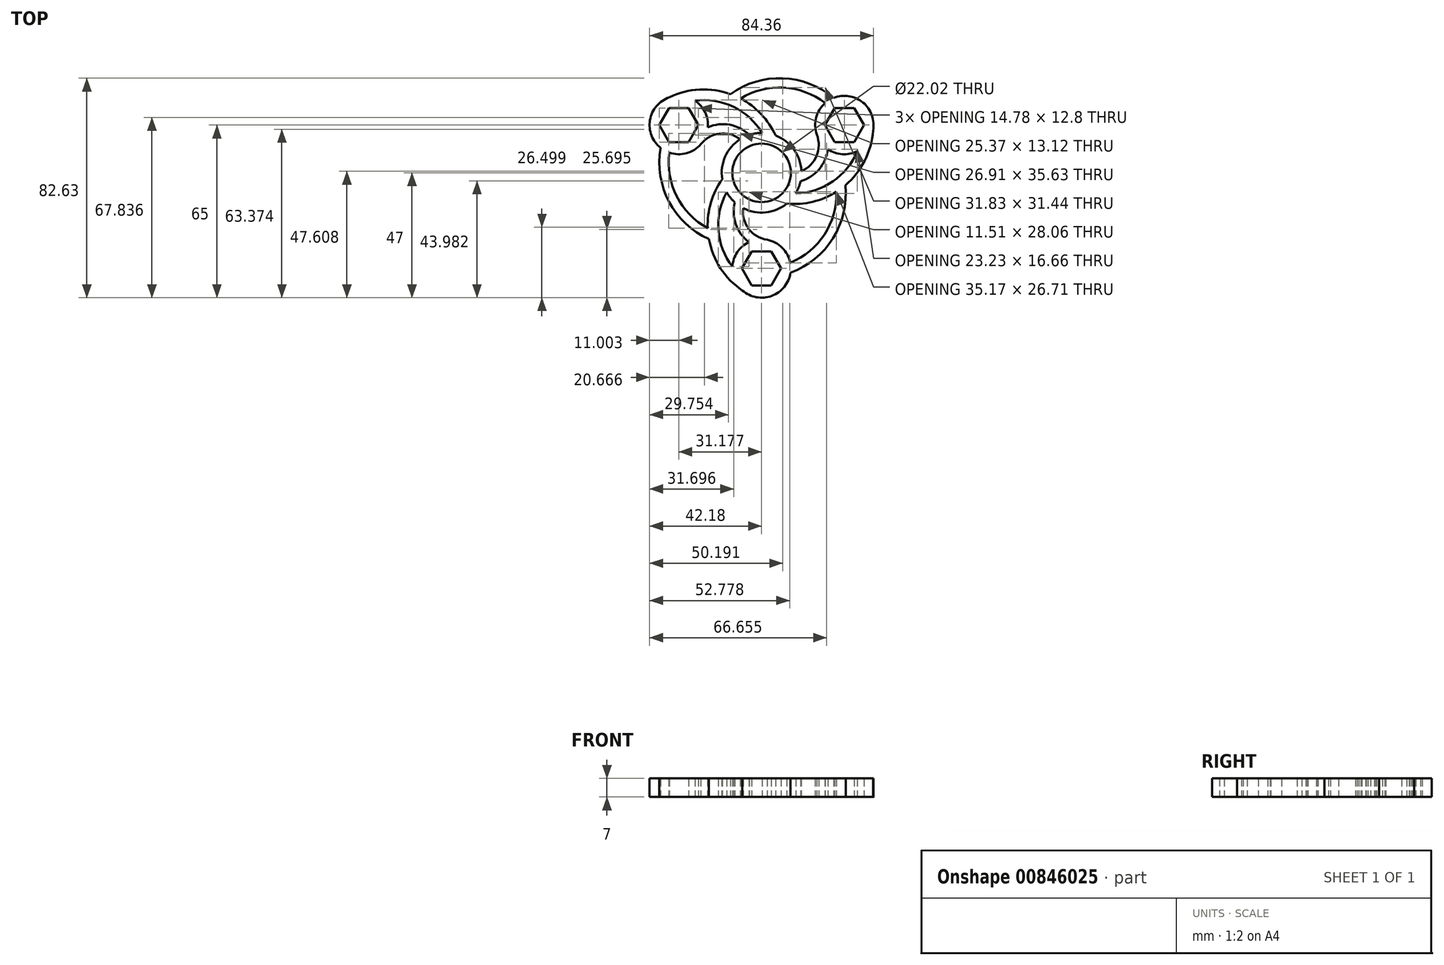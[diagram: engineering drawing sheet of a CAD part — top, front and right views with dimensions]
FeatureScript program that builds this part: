
annotation { "Feature Type Name" : "Feature", "Feature Type Description" : "" }
export const myFeature = defineFeature(function(context is Context, id is Id, definition is map)
    precondition{}
    {
        {
            var Q0;
            Q0=qCreatedBy(makeId("Top.planeOp"),FACE);
            var sketch = newSketch(context, id + "F0", { "sketchPlane" : qUnion([Q0])});
            skCircle(sketch, "E0", {"center": v(0, 0) * mm, "radius": 11.01 * mm});
            skCircle(sketch, "E1", {"center": v(0, 0) * mm, "radius": 15 * mm});
            skCircle(sketch, "E2", {"center": v(0, -36) * mm, "radius": 11 * mm});
            skCircle(sketch, "E3.1.0", {"center": v(31.18, 18) * mm, "radius": 11 * mm});
            skCircle(sketch, "E3.2.0", {"center": v(-31.18, 18) * mm, "radius": 11 * mm});
            skArc(sketch, "E4", {"start": v(5.28, 14.04) * mm, "mid": v(-11.7, 29.65) * mm, "end": v(-34.73, 28.41) * mm});
            skArc(sketch, "E5.0", {"start": v(2.32, 10.76) * mm, "mid": v(-8.54, 23.75) * mm, "end": v(-25.11, 27.18) * mm});
            skArc(sketch, "E6.1.0", {"start": v(-14.8, -2.44) * mm, "mid": v(-19.83, -24.95) * mm, "end": v(-7.24, -44.28) * mm});
            skArc(sketch, "E6.1.1", {"start": v(-10.48, -3.37) * mm, "mid": v(-16.3, -19.27) * mm, "end": v(-10.98, -35.33) * mm});
            skArc(sketch, "E6.2.0", {"start": v(9.52, -11.6) * mm, "mid": v(31.52, -4.7) * mm, "end": v(41.97, 15.87) * mm});
            skArc(sketch, "E6.2.1", {"start": v(8.16, -7.39) * mm, "mid": v(24.83, -4.48) * mm, "end": v(36.09, 8.16) * mm});
            skArc(sketch, "E7", {"start": v(-4.6, 14.28) * mm, "mid": v(-11.97, 18.1) * mm, "end": v(-20.21, 17.13) * mm});
            skArc(sketch, "E8.0", {"start": v(-8.06, 12.65) * mm, "mid": v(-15.85, 14.74) * mm, "end": v(-22.88, 10.78) * mm});
            skArc(sketch, "E9.1.0", {"start": v(-10.06, -11.12) * mm, "mid": v(-9.69, -19.41) * mm, "end": v(-4.73, -26.07) * mm});
            skArc(sketch, "E9.1.1", {"start": v(-6.93, -13.3) * mm, "mid": v(-4.84, -21.1) * mm, "end": v(2.1, -25.2) * mm});
            skArc(sketch, "E9.2.0", {"start": v(14.66, -3.15) * mm, "mid": v(21.65, 1.32) * mm, "end": v(24.94, 8.94) * mm});
            skArc(sketch, "E9.2.1", {"start": v(14.99, 0.66) * mm, "mid": v(20.7, 6.36) * mm, "end": v(20.77, 14.42) * mm});
            skArc(sketch, "E10", {"start": v(-37.98, 9.36) * mm, "mid": v(-34.81, -10.93) * mm, "end": v(-19.83, -24.96) * mm});
            skArc(sketch, "E11.0", {"start": v(-34.72, 7.59) * mm, "mid": v(-31.93, -8.88) * mm, "end": v(-20.28, -20.83) * mm});
            skArc(sketch, "E12.1.0", {"start": v(10.79, -33.86) * mm, "mid": v(23.65, -23.21) * mm, "end": v(28.18, -7.14) * mm});
            skArc(sketch, "E12.1.1", {"start": v(10.89, -37.57) * mm, "mid": v(26.87, -24.68) * mm, "end": v(31.53, -4.7) * mm});
            skArc(sketch, "E12.2.0", {"start": v(23.93, 26.27) * mm, "mid": v(8.28, 32.1) * mm, "end": v(-7.9, 27.98) * mm});
            skArc(sketch, "E12.2.1", {"start": v(27.1, 28.21) * mm, "mid": v(7.94, 35.61) * mm, "end": v(-11.7, 29.65) * mm});
            skCircle(sketch, "E13.cCircle", {"center": v(-31.18, 18) * mm, "radius": 6.4 * mm, "construction": true});
            skLineSegment(sketch, "E13.0", {"start": v(-23.79, 18) * mm, "end": v(-27.48, 11.6) * mm});
            skLineSegment(sketch, "E13.1", {"start": v(-27.48, 11.6) * mm, "end": v(-34.87, 11.6) * mm});
            skLineSegment(sketch, "E13.2", {"start": v(-34.87, 11.6) * mm, "end": v(-38.57, 18) * mm});
            skLineSegment(sketch, "E13.3", {"start": v(-38.57, 18) * mm, "end": v(-34.87, 24.4) * mm});
            skLineSegment(sketch, "E13.4", {"start": v(-34.87, 24.4) * mm, "end": v(-27.48, 24.4) * mm});
            skLineSegment(sketch, "E13.5", {"start": v(-27.48, 24.4) * mm, "end": v(-23.79, 18) * mm});
            skPoint(sketch, "E13.0.midPoint", {"position": v(-25.63, 14.8) * mm});
            skCircle(sketch, "E14.1.0", {"center": v(0, -36) * mm, "radius": 6.4 * mm, "construction": true});
            skLineSegment(sketch, "E14.1.1", {"start": v(-3.7, -42.4) * mm, "end": v(-7.4, -36) * mm});
            skLineSegment(sketch, "E14.1.2", {"start": v(3.7, -42.4) * mm, "end": v(-3.7, -42.4) * mm});
            skLineSegment(sketch, "E14.1.3", {"start": v(7.4, -36) * mm, "end": v(3.7, -42.4) * mm});
            skLineSegment(sketch, "E14.1.4", {"start": v(3.7, -29.6) * mm, "end": v(7.4, -36) * mm});
            skLineSegment(sketch, "E14.1.5", {"start": v(-3.7, -29.6) * mm, "end": v(3.7, -29.6) * mm});
            skLineSegment(sketch, "E14.1.6", {"start": v(-7.4, -36) * mm, "end": v(-3.7, -29.6) * mm});
            skCircle(sketch, "E14.2.0", {"center": v(31.18, 18) * mm, "radius": 6.4 * mm, "construction": true});
            skLineSegment(sketch, "E14.2.1", {"start": v(38.57, 18) * mm, "end": v(34.87, 11.6) * mm});
            skLineSegment(sketch, "E14.2.2", {"start": v(34.87, 24.4) * mm, "end": v(38.57, 18) * mm});
            skLineSegment(sketch, "E14.2.3", {"start": v(27.48, 24.4) * mm, "end": v(34.87, 24.4) * mm});
            skLineSegment(sketch, "E14.2.4", {"start": v(23.79, 18) * mm, "end": v(27.48, 24.4) * mm});
            skLineSegment(sketch, "E14.2.5", {"start": v(27.48, 11.6) * mm, "end": v(23.79, 18) * mm});
            skLineSegment(sketch, "E14.2.6", {"start": v(34.87, 11.6) * mm, "end": v(27.48, 11.6) * mm});
            skSolve(sketch);
        }
        {
            var Q0;
            {var subQ0=sQuery(id+"F0.wireOp",EDGE,"E3.2.0");var subQ1=makeQuery(id+"F0.imprint","INTERSECT",VERTEX,{"derivedFrom":[subQ0,sQuery(id+"F0.wireOp",EDGE,"E7")]});Q0=makeQuery(id+"F0.imprint","IMPRINT",FACE,{"disambiguationData":[TD([[makeQuery(id+"F0.imprint","IMPRINT",EDGE,{"disambiguationData":[TD([[subQ1,1.0]])],"derivedFrom":subQ0}),1.0]])]});}
            var Q1;
            {var subQ0=sQuery(id+"F0.wireOp",EDGE,"E4");Q1=makeQuery(id+"F0.imprint","IMPRINT",FACE,{"disambiguationData":[TD([[makeQuery(id+"F0.imprint","IMPRINT",EDGE,{"derivedFrom":subQ0}),1.0]])]});}
            var Q2;
            {var subQ4=sQuery(id+"F0.wireOp",EDGE,"E5.0");var subQ6=sQuery(id+"F0.wireOp",EDGE,"E0");var subQ7=makeQuery(id+"F0.imprint","INTERSECT",VERTEX,{"derivedFrom":[subQ6,subQ4]});Q2=makeQuery(id+"F0.imprint","IMPRINT",FACE,{"disambiguationData":[TD([[makeQuery(id+"F0.imprint","IMPRINT",EDGE,{"disambiguationData":[TD([[subQ7,-1.0]])],"derivedFrom":subQ6}),-1.0]])]});}
            var Q3;
            {var subQ0=sQuery(id+"F0.wireOp",EDGE,"E5.0");var subQ1=sQuery(id+"F0.wireOp",EDGE,"E0");var subQ2=makeQuery(id+"F0.imprint","INTERSECT",VERTEX,{"derivedFrom":[subQ1,subQ0]});Q3=makeQuery(id+"F0.imprint","IMPRINT",FACE,{"disambiguationData":[TD([[makeQuery(id+"F0.imprint","IMPRINT",EDGE,{"disambiguationData":[TD([[subQ2,1.0]])],"derivedFrom":subQ1}),-1.0]])]});}
            var Q4;
            {var subQ4=sQuery(id+"F0.wireOp",EDGE,"E6.1.1");var subQ5=sQuery(id+"F0.wireOp",EDGE,"E0");var subQ6=makeQuery(id+"F0.imprint","INTERSECT",VERTEX,{"derivedFrom":[subQ5,subQ4]});Q4=makeQuery(id+"F0.imprint","IMPRINT",FACE,{"disambiguationData":[TD([[makeQuery(id+"F0.imprint","IMPRINT",EDGE,{"disambiguationData":[TD([[subQ6,-1.0]])],"derivedFrom":subQ5}),-1.0]])]});}
            var Q5;
            {var subQ0=sQuery(id+"F0.wireOp",EDGE,"E6.1.0");Q5=makeQuery(id+"F0.imprint","IMPRINT",FACE,{"disambiguationData":[TD([[makeQuery(id+"F0.imprint","IMPRINT",EDGE,{"derivedFrom":subQ0}),1.0]])]});}
            var Q6;
            {var subQ0=sQuery(id+"F0.wireOp",EDGE,"E7");Q6=makeQuery(id+"F0.imprint","IMPRINT",FACE,{"disambiguationData":[TD([[makeQuery(id+"F0.imprint","IMPRINT",EDGE,{"derivedFrom":subQ0}),1.0]])]});}
            var Q7;
            {var subQ0=sQuery(id+"F0.wireOp",EDGE,"E6.2.0");Q7=makeQuery(id+"F0.imprint","IMPRINT",FACE,{"disambiguationData":[TD([[makeQuery(id+"F0.imprint","IMPRINT",EDGE,{"derivedFrom":subQ0}),1.0]])]});}
            var Q8;
            {var subQ0=sQuery(id+"F0.wireOp",EDGE,"E3.1.0");var subQ1=makeQuery(id+"F0.imprint","INTERSECT",VERTEX,{"derivedFrom":[subQ0,sQuery(id+"F0.wireOp",EDGE,"E6.2.0")]});Q8=makeQuery(id+"F0.imprint","IMPRINT",FACE,{"disambiguationData":[TD([[makeQuery(id+"F0.imprint","IMPRINT",EDGE,{"disambiguationData":[TD([[subQ1,1.0]])],"derivedFrom":subQ0}),1.0]])]});}
            var Q9;
            {var subQ0=sQuery(id+"F0.wireOp",EDGE,"E2");var subQ1=makeQuery(id+"F0.imprint","INTERSECT",VERTEX,{"derivedFrom":[subQ0,sQuery(id+"F0.wireOp",EDGE,"E6.1.0")]});Q9=makeQuery(id+"F0.imprint","IMPRINT",FACE,{"disambiguationData":[TD([[makeQuery(id+"F0.imprint","IMPRINT",EDGE,{"disambiguationData":[TD([[subQ1,1.0]])],"derivedFrom":subQ0}),1.0]])]});}
            var Q10;
            {var subQ0=sQuery(id+"F0.wireOp",EDGE,"E9.2.0");Q10=makeQuery(id+"F0.imprint","IMPRINT",FACE,{"disambiguationData":[TD([[makeQuery(id+"F0.imprint","IMPRINT",EDGE,{"derivedFrom":subQ0}),1.0]])]});}
            var Q11;
            {var subQ0=sQuery(id+"F0.wireOp",EDGE,"E9.1.0");Q11=makeQuery(id+"F0.imprint","IMPRINT",FACE,{"disambiguationData":[TD([[makeQuery(id+"F0.imprint","IMPRINT",EDGE,{"derivedFrom":subQ0}),1.0]])]});}
            var Q12;
            {var subQ0=sQuery(id+"F0.wireOp",EDGE,"E10");Q12=makeQuery(id+"F0.imprint","IMPRINT",FACE,{"disambiguationData":[TD([[makeQuery(id+"F0.imprint","IMPRINT",EDGE,{"derivedFrom":subQ0}),1.0]])]});}
            var Q13;
            {var subQ0=sQuery(id+"F0.wireOp",EDGE,"E12.2.0");Q13=makeQuery(id+"F0.imprint","IMPRINT",FACE,{"disambiguationData":[TD([[makeQuery(id+"F0.imprint","IMPRINT",EDGE,{"derivedFrom":subQ0}),-1.0]])]});}
            var Q14;
            {var subQ0=sQuery(id+"F0.wireOp",EDGE,"E12.1.0");Q14=makeQuery(id+"F0.imprint","IMPRINT",FACE,{"disambiguationData":[TD([[makeQuery(id+"F0.imprint","IMPRINT",EDGE,{"derivedFrom":subQ0}),-1.0]])]});}
            extrude(context, id + "F1", {"entities" : qUnion([Q0, Q1, Q2, Q3, Q4, Q5, Q6, Q7, Q8, Q9, Q10, Q11, Q12, Q13, Q14]), "depth" : 7 * mm, "offsetDistance" : 25 * mm});
        }
    });
